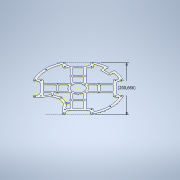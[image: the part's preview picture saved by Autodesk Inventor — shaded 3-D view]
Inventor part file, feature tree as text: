
AUTODESK INVENTOR PART (.ipt)
format: ipt  version: 2020 (Build 240168000, 168)  size: 1,359,872 bytes
history: native  units: mm
features: extrude x9, sketch x8, projected_geometry x6, other x1
ambient origin geometry x8: Origin, YZ Plane, XZ Plane, XY Plane, X Axis, Y Axis, Z Axis, Center Point
bodies: Body1 (feature_tree)
feature tree (24):
  other  "Твердое тело1"
  extrude  "outer"  TaperAngle=45.0deg  [1 undecoded]
  extrude  "inner"  Depth=7.0mm
  sketch  "Эскиз3"
  extrude  "Выдавливание3"  Depth=20.0mm
  extrude  "Выдавливание4"  Depth=7.0mm
  extrude  "Выдавливание5"  Depth=3.2mm
  sketch  "Эскиз5"
  extrude  "Выдавливание7"  Depth=59.0mm
  extrude  "Выдавливание8"  Depth=83.0mm
  sketch  "Эскиз6"
  extrude  "Выдавливание9"  Depth=69.0mm
  extrude  "Выдавливание10"  Depth=55.0mm
  sketch  "Эскиз7"
  sketch  "Эскиз8"
  sketch  "Эскиз1"
  sketch  "Эскиз2"
  projected_geometry  "Спроецированная петля1"
  projected_geometry  "Спроецированная петля2"
  sketch  "Эскиз4"
  projected_geometry  "Спроецированная петля3"
  projected_geometry  "Спроецированная петля4"
  projected_geometry  "Спроецированная петля5"
  projected_geometry  "Спроецированная петля6"
note: 1 required parameter value undecoded (feature->parameter linkage not recoverable at this tier; creation-order binding heuristic only, values carry confidence <= 0.55)
